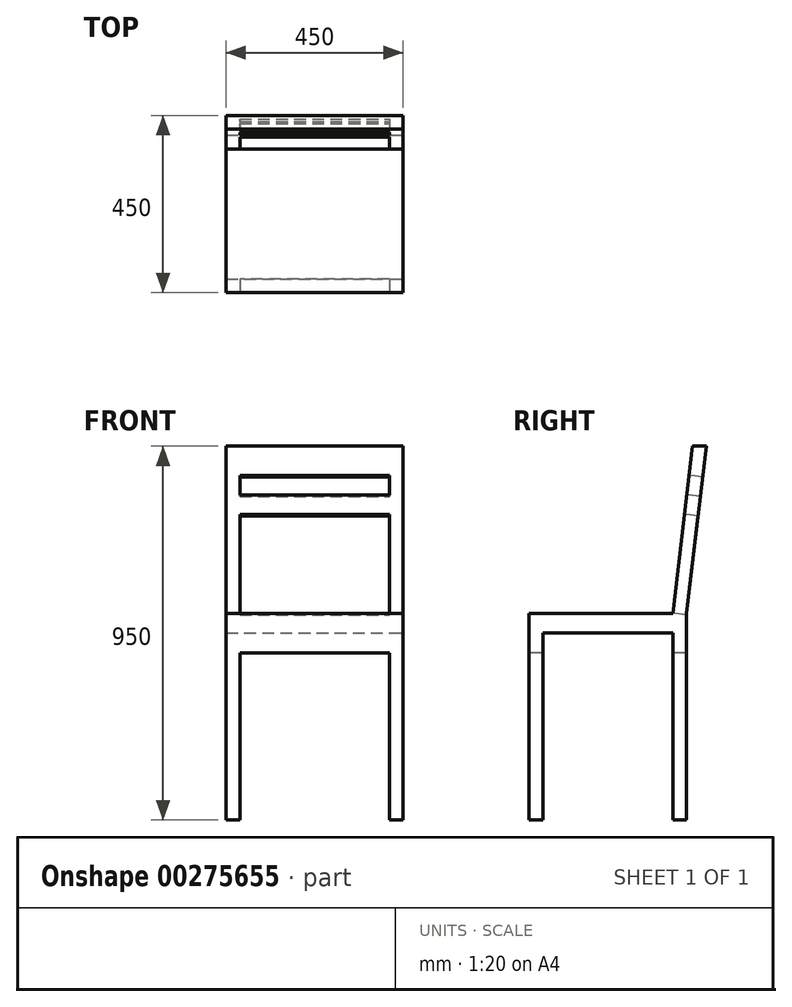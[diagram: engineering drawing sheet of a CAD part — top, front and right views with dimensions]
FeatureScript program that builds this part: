
annotation { "Feature Type Name" : "Feature", "Feature Type Description" : "" }
export const myFeature = defineFeature(function(context is Context, id is Id, definition is map)
    precondition{}
    {
        {
            var Q0;
            Q0=qCreatedBy(makeId("Top.planeOp"),FACE);
            var sketch = newSketch(context, id + "F0", { "sketchPlane" : qUnion([Q0])});
            skLineSegment(sketch, "E0.bottom", {"start": v(225, 225) * mm, "end": v(-225, 225) * mm});
            skLineSegment(sketch, "E0.top", {"start": v(225, -225) * mm, "end": v(-225, -225) * mm});
            skLineSegment(sketch, "E0.left", {"start": v(225, 225) * mm, "end": v(225, -225) * mm});
            skLineSegment(sketch, "E0.right", {"start": v(-225, 225) * mm, "end": v(-225, -225) * mm});
            skPoint(sketch, "E0.middle", {"position": v(0, 0) * mm});
            skSolve(sketch);
        }
        {
            var Q0;
            Q0=qSketchRegion(id+"F0",true);
            extrude(context, id + "F1", {"entities" : qUnion([Q0]), "depth" : 950 * mm});
        }
        {
            var Q0;
            Q0=makeQuery(id+"F1.opExtrude","SWEPT_FACE",FACE,{"disambiguationData":[OSD([sQuery(id+"F0.wireOp",EDGE,"E0.left")])]});
            var sketch = newSketch(context, id + "F2", { "sketchPlane" : qUnion([Q0])});
            skLineSegment(sketch, "E1.bottom", {"start": v(-225, 525) * mm, "end": v(225, 525) * mm});
            skLineSegment(sketch, "E1.top", {"start": v(-225, 475) * mm, "end": v(225, 475) * mm});
            skLineSegment(sketch, "E1.left", {"start": v(-225, 525) * mm, "end": v(-225, 475) * mm});
            skLineSegment(sketch, "E1.right", {"start": v(225, 525) * mm, "end": v(225, 475) * mm});
            skLineSegment(sketch, "E2", {"start": v(225, 950) * mm, "end": v(175, 525) * mm});
            skLineSegment(sketch, "E3", {"start": v(190, 950) * mm, "end": v(140, 525) * mm});
            skLineSegment(sketch, "E4", {"start": v(140, 525) * mm, "end": v(140, 0) * mm});
            skLineSegment(sketch, "E5", {"start": v(175, 525) * mm, "end": v(175, 0) * mm});
            skLineSegment(sketch, "E6.bottom", {"start": v(-225, 0) * mm, "end": v(-190, 0) * mm});
            skLineSegment(sketch, "E6.top", {"start": v(-225, 475) * mm, "end": v(-190, 475) * mm});
            skLineSegment(sketch, "E6.left", {"start": v(-225, 0) * mm, "end": v(-225, 475) * mm});
            skLineSegment(sketch, "E6.right", {"start": v(-190, 0) * mm, "end": v(-190, 475) * mm});
            skSolve(sketch);
        }
        {
            var Q0;
            {var subQ4=sQuery(id+"F2.wireOp",EDGE,"E3");Q0=makeQuery(id+"F2.imprint","IMPRINT",FACE,{"disambiguationData":[TD([[makeQuery(id+"F2.imprint","IMPRINT",EDGE,{"derivedFrom":subQ4}),-1.0]])]});}
            var Q1;
            {var subQ0=sQuery(id+"F2.wireOp",EDGE,"E6.right");Q1=makeQuery(id+"F2.imprint","IMPRINT",FACE,{"disambiguationData":[TD([[makeQuery(id+"F2.imprint","IMPRINT",EDGE,{"derivedFrom":subQ0}),-1.0]])]});}
            var Q2;
            {var subQ4=sQuery(id+"F2.wireOp",EDGE,"E2");Q2=makeQuery(id+"F2.imprint","IMPRINT",FACE,{"disambiguationData":[TD([[makeQuery(id+"F2.imprint","IMPRINT",EDGE,{"derivedFrom":subQ4}),1.0]])]});}
            var Q3;
            {var subQ1=sQuery(id+"F0.wireOp",EDGE,"E0.left");var subQ4=sQuery(id+"F2.wireOp",EDGE,"E5");var subQ6=makeQuery(id+"F1.opExtrude","CAP_EDGE",EDGE,{"disambiguationData":[OSD([subQ1])],"isStart":true});var subQ7=makeQuery(id+"F2.imprint","INTERSECT",VERTEX,{"derivedFrom":[subQ6,subQ4]});Q3=makeQuery(id+"F2.imprint","IMPRINT",FACE,{"disambiguationData":[TD([[makeQuery(id+"F2.imprint","IMPRINT",EDGE,{"disambiguationData":[TD([[subQ7,1.0]])],"derivedFrom":subQ4}),1.0]])]});}
            var Q4;
            {var subQ0=sQuery(id+"F2.wireOp",EDGE,"E1.right");Q4=makeQuery(id+"F2.imprint","IMPRINT",FACE,{"disambiguationData":[TD([[makeQuery(id+"F2.imprint","IMPRINT",EDGE,{"derivedFrom":subQ0}),-1.0]])]});}
            extrude(context, id + "F3", {"entities" : qUnion([Q0, Q1, Q2, Q3, Q4]), "operationType" : NewBodyOperationType.REMOVE, "endBound" : BoundingType.THROUGH_ALL, "oppositeDirection" : true, "depth" : 25 * mm});
        }
        {
            var Q0;
            Q0=makeQuery(id+"F1.opExtrude","SWEPT_FACE",FACE,{"disambiguationData":[OSD([sQuery(id+"F0.wireOp",EDGE,"E0.top")])]});
            var sketch = newSketch(context, id + "F4", { "sketchPlane" : qUnion([Q0])});
            skLineSegment(sketch, "E7", {"start": v(-190, 0) * mm, "end": v(-190, 425) * mm});
            skLineSegment(sketch, "E8", {"start": v(-190, 425) * mm, "end": v(190, 425) * mm});
            skLineSegment(sketch, "E9", {"start": v(190, 425) * mm, "end": v(190, 0) * mm});
            skSolve(sketch);
        }
        {
            var Q0;
            Q0 = qSketchRegion(id + "F4", true);
            var Q1;
            {var subQ0=sQuery(id+"F4.wireOp",EDGE,"E7");Q1=makeQuery(id+"F4.imprint","IMPRINT",FACE,{"disambiguationData":[TD([[makeQuery(id+"F4.imprint","IMPRINT",EDGE,{"derivedFrom":subQ0}),-1.0]])]});}
            extrude(context, id + "F5", {"entities" : qUnion([Q0, Q1]), "operationType" : NewBodyOperationType.REMOVE, "endBound" : BoundingType.THROUGH_ALL, "oppositeDirection" : true, "depth" : 25 * mm});
        }
        {
            var Q0;
            Q0=makeQuery(id+"F3.boolean.opBoolean","COPY",FACE,{"derivedFrom":makeQuery(id+"F3.opExtrude","SWEPT_FACE",FACE,{"disambiguationData":[OSD([sQuery(id+"F2.wireOp",EDGE,"E3")])]})});
            var sketch = newSketch(context, id + "F6", { "sketchPlane" : qUnion([Q0])});
            skLineSegment(sketch, "E10", {"start": v(-190, 537.76) * mm, "end": v(-190, 890.7) * mm});
            skLineSegment(sketch, "E11", {"start": v(-190, 890.7) * mm, "end": v(190, 890.7) * mm});
            skLineSegment(sketch, "E12", {"start": v(190, 890.7) * mm, "end": v(190, 537.76) * mm});
            skLineSegment(sketch, "E13", {"start": v(-190, 840.7) * mm, "end": v(190, 840.7) * mm});
            skLineSegment(sketch, "E14", {"start": v(-190, 790.7) * mm, "end": v(190, 790.7) * mm});
            skPoint(sketch, "E14.startSnap0", {"position": v(-225, 790.7) * mm});
            skSolve(sketch);
        }
        {
            var Q0;
            {var subQ0=sQuery(id+"F6.wireOp",EDGE,"E11");Q0=makeQuery(id+"F6.imprint","IMPRINT",FACE,{"disambiguationData":[TD([[makeQuery(id+"F6.imprint","IMPRINT",EDGE,{"derivedFrom":subQ0}),-1.0]])]});}
            var Q1;
            {var subQ3=sQuery(id+"F6.wireOp",EDGE,"E14");Q1=makeQuery(id+"F6.imprint","IMPRINT",FACE,{"disambiguationData":[TD([[makeQuery(id+"F6.imprint","IMPRINT",EDGE,{"derivedFrom":subQ3}),-1.0]])]});}
            extrude(context, id + "F7", {"entities" : qUnion([Q0, Q1]), "operationType" : NewBodyOperationType.REMOVE, "endBound" : BoundingType.THROUGH_ALL, "oppositeDirection" : true, "depth" : 25 * mm});
        }
    });
